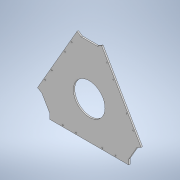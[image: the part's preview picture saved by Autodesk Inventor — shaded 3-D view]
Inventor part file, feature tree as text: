
AUTODESK INVENTOR PART (.ipt)
format: ipt  version: 2020 (Build 240168000, 168)  size: 134,144 bytes
history: native  units: in
note: dims shown in document units (in); Inventor stores cm internally (conversion verified against a paired STEP export)
features: extrude x1, sketch x1
ambient origin geometry x8: Origin, YZ Plane, XZ Plane, XY Plane, X Axis, Y Axis, Z Axis, Center Point
bodies: Solid1 (feature_tree)
feature tree (2):
  extrude  "Extrusion1"  [1 undecoded]
  sketch  "Sketch1"  dims[d0=0.4375in d1=0.0in]
note: 1 required parameter value undecoded (feature->parameter linkage not recoverable at this tier; creation-order binding heuristic only, values carry confidence <= 0.55)
